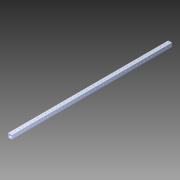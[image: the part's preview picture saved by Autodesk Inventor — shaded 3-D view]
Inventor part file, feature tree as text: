
AUTODESK INVENTOR PART (.ipt)
format: ipt  version: 2014 SP1 (Build 180222100, 222)  size: 1,371,136 bytes
history: native  units: in
note: dims shown in document units (in); Inventor stores cm internally (conversion verified against a paired STEP export)
features: pattern_circular x1, other x1, extrude x1, imported_body x1, sketch x1
ambient origin geometry x8: Origin, YZ Plane, XZ Plane, XY Plane, X Axis, Y Axis, Z Axis, Center Point
bodies: Body1 (feature_tree)
feature tree (5):
  pattern_circular  "CirPattern2"
  other  "1x1 tube1"
  extrude  "Extrusion1"  [1 undecoded]
  imported_body  "Base1"
  sketch  "Sketch1"  dims[d0=16.0in d1=0.0in]
note: 1 required parameter value undecoded (feature->parameter linkage not recoverable at this tier; creation-order binding heuristic only, values carry confidence <= 0.55)
